AUTODESK INVENTOR PART (.ipt)
format: ipt  version: 2019.4 (Build 234330000, 330)  size: 110,080 bytes
history: native  units: in
note: dims shown in document units (in); Inventor stores cm internally (conversion verified against a paired STEP export)
features: sketch x1
ambient origin geometry x8: Origin, YZ Plane, XZ Plane, XY Plane, X Axis, Y Axis, Z Axis, Center Point
feature tree (1):
  sketch  "Sketch1"  dims[d0=0.1181in d18=0.0787in d19=0.0756in d20=0.2756in d21=0.0787in d22=90.0deg d24=0.2362in d32=0.0458in d33=0.0071in d34=0.0071in d35=0.0197in d37=0.0315in d38=0.0079in d39=0.0039in]
